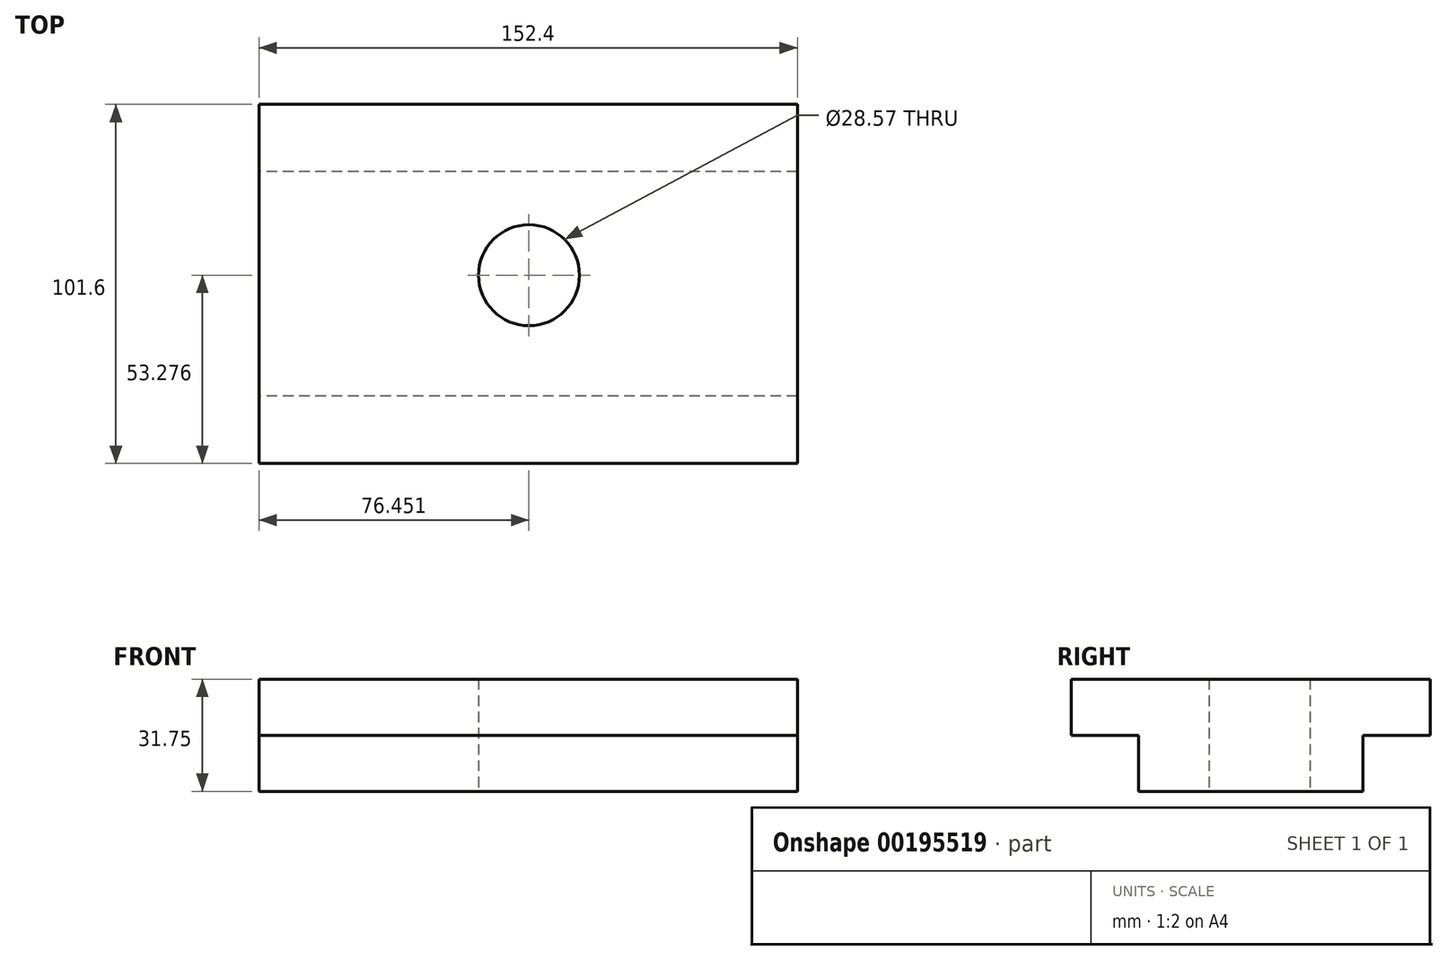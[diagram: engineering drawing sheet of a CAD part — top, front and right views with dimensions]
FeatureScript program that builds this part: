
annotation { "Feature Type Name" : "Feature", "Feature Type Description" : "" }
export const myFeature = defineFeature(function(context is Context, id is Id, definition is map)
    precondition{}
    {
        {
            var Q0;
            Q0=qCreatedBy(makeId("Top.planeOp"),FACE);
            var sketch = newSketch(context, id + "F0", { "sketchPlane" : qUnion([Q0])});
            skLineSegment(sketch, "E0", {"start": v(-75.14, 9.62) * mm, "end": v(77.26, 9.62) * mm});
            skLineSegment(sketch, "E1", {"start": v(77.26, 9.62) * mm, "end": v(77.26, -53.88) * mm});
            skLineSegment(sketch, "E2", {"start": v(77.26, -53.88) * mm, "end": v(-75.14, -53.88) * mm});
            skLineSegment(sketch, "E3", {"start": v(-75.14, -53.88) * mm, "end": v(-75.14, 9.62) * mm});
            skSolve(sketch);
        }
        {
            var Q0;
            Q0=makeQuery(id+"F0.imprint","IMPRINT",FACE,{"disambiguationData":[TD([[makeQuery(id+"F0.imprint","IMPRINT",EDGE,{"derivedFrom":sQuery(id+"F0.wireOp",EDGE,"E0")}),-1.0]])]});
            extrude(context, id + "F1", {"entities" : qUnion([Q0]), "depth" : 31.75 * mm});
        }
        {
            var Q0;
            Q0=makeQuery(id+"F1.opExtrude","SWEPT_FACE",FACE,{"disambiguationData":[OSD([sQuery(id+"F0.wireOp",EDGE,"E0")])]});
            var sketch = newSketch(context, id + "F2", { "sketchPlane" : qUnion([Q0])});
            skLineSegment(sketch, "E4", {"start": v(-77.26, 15.88) * mm, "end": v(75.14, 15.88) * mm});
            skSolve(sketch);
        }
        {
            var Q0;
            Q0=makeQuery(id+"F1.opExtrude","SWEPT_FACE",FACE,{"disambiguationData":[OSD([sQuery(id+"F0.wireOp",EDGE,"E2")])]});
            var sketch = newSketch(context, id + "F3", { "sketchPlane" : qUnion([Q0])});
            skLineSegment(sketch, "E5", {"start": v(77.26, 15.88) * mm, "end": v(-75.14, 15.88) * mm});
            skSolve(sketch);
        }
        {
            var Q0;
            {var subQ0=sQuery(id+"F3.wireOp",EDGE,"E5");Q0=makeQuery(id+"F3.imprint","IMPRINT",FACE,{"disambiguationData":[TD([[makeQuery(id+"F3.imprint","IMPRINT",EDGE,{"derivedFrom":subQ0}),-1.0]])]});}
            extrude(context, id + "F4", {"entities" : qUnion([Q0]), "operationType" : NewBodyOperationType.ADD, "depth" : 19.05 * mm});
        }
        {
            var Q0;
            {var subQ0=sQuery(id+"F2.wireOp",EDGE,"E4");Q0=makeQuery(id+"F2.imprint","IMPRINT",FACE,{"disambiguationData":[TD([[makeQuery(id+"F2.imprint","IMPRINT",EDGE,{"derivedFrom":subQ0}),1.0]])]});}
            extrude(context, id + "F5", {"entities" : qUnion([Q0]), "operationType" : NewBodyOperationType.ADD, "depth" : 19.05 * mm});
        }
        {
            var Q0;
            Q0=makeQuery(id+"F1.opExtrude","CAP_FACE",FACE,{"disambiguationData":[OSD([sQuery(id+"F0.wireOp",EDGE,"E0"),sQuery(id+"F0.wireOp",EDGE,"E1"),sQuery(id+"F0.wireOp",EDGE,"E2"),sQuery(id+"F0.wireOp",EDGE,"E3")])],"isStart":true});
            var sketch = newSketch(context, id + "F6", { "sketchPlane" : qUnion([Q0])});
            skSolve(sketch);
        }
        {
            var Q0;
            Q0=makeQuery(id+"F6.imprint","IMPRINT",FACE,{"disambiguationData":[TD([[makeQuery(id+"F6.imprint","IMPRINT",EDGE,{"derivedFrom":makeQuery(id+"F1.opExtrude","CAP_EDGE",EDGE,{"disambiguationData":[OSD([sQuery(id+"F0.wireOp",EDGE,"E0")])],"isStart":true})}),1.0]])]});
            var sketch = newSketch(context, id + "F7", { "sketchPlane" : qUnion([Q0])});
            skCircle(sketch, "E6", {"center": v(1.31, 19.65) * mm, "radius": 14.29 * mm});
            skSolve(sketch);
        }
        {
            var Q0;
            Q0=makeQuery(id+"F7.imprint","IMPRINT",FACE,{"disambiguationData":[TD([[makeQuery(id+"F7.imprint","IMPRINT",EDGE,{"derivedFrom":sQuery(id+"F7.wireOp",EDGE,"E6")}),1.0]])]});
            extrude(context, id + "F8", {"entities" : qUnion([Q0]), "operationType" : NewBodyOperationType.REMOVE, "endBound" : BoundingType.THROUGH_ALL, "oppositeDirection" : true, "depth" : 25.4 * mm});
        }
    });
